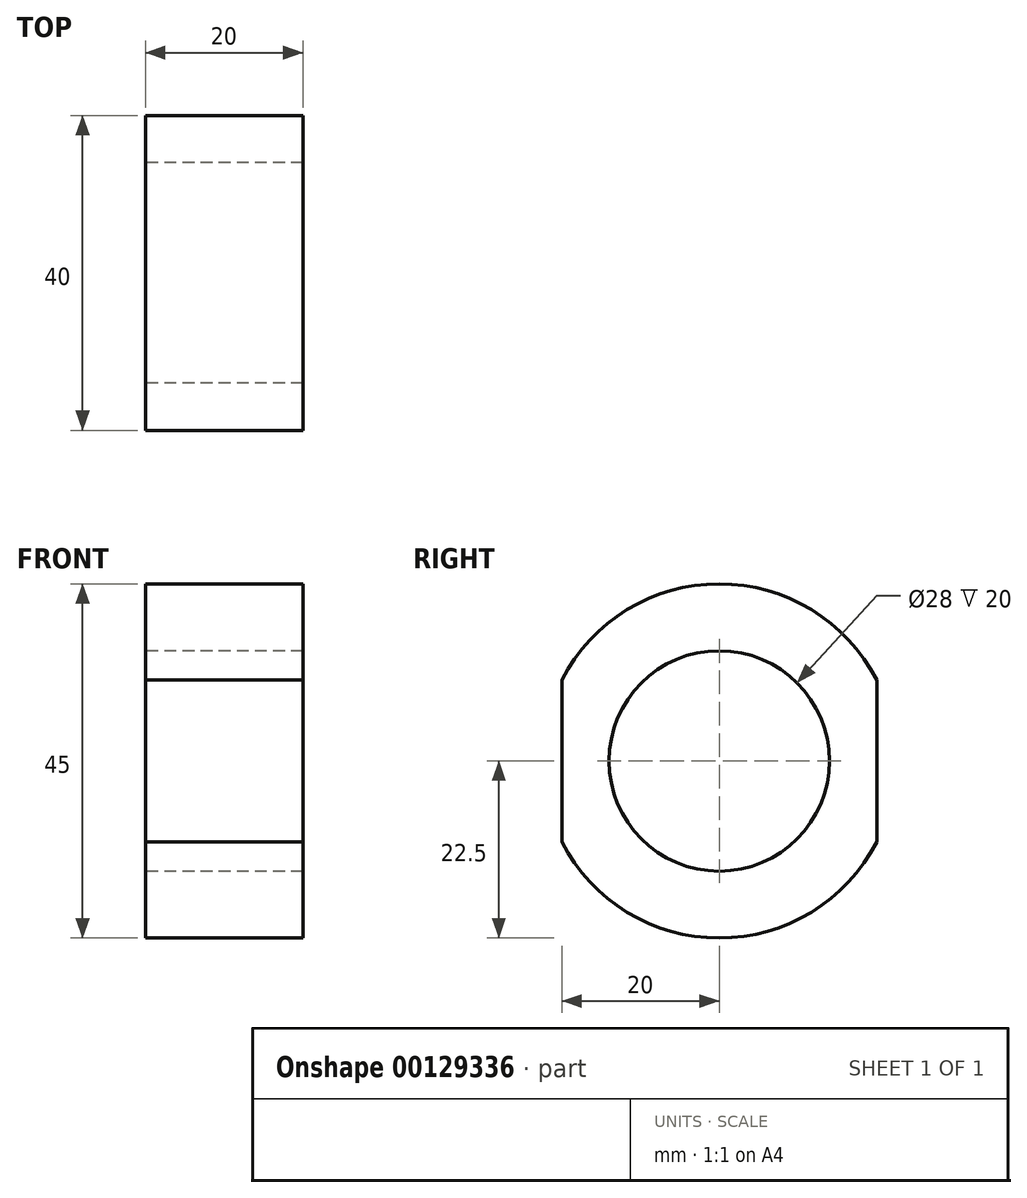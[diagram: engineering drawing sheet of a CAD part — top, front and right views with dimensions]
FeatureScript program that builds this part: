
annotation { "Feature Type Name" : "Feature", "Feature Type Description" : "" }
export const myFeature = defineFeature(function(context is Context, id is Id, definition is map)
    precondition{}
    {
        {
            var Q0;
            Q0=qCreatedBy(makeId("Right.planeOp"),FACE);
            var sketch = newSketch(context, id + "F0", { "sketchPlane" : qUnion([Q0])});
            skCircle(sketch, "E0", {"center": v(0, 0) * mm, "radius": 14 * mm});
            skArc(sketch, "E1", {"start": v(-20, -10.3) * mm, "mid": v(0, -22.5) * mm, "end": v(20, -10.3) * mm});
            skLineSegment(sketch, "E2", {"start": v(-20, 10.3) * mm, "end": v(-20, -10.3) * mm});
            skPoint(sketch, "E3.orphan", {"position": v(-20, 30.88) * mm});
            skLineSegment(sketch, "E4.MirrorCS", {"start": v(20, 10.3) * mm, "end": v(20, -10.3) * mm});
            skArc(sketch, "E5.trimOffspring", {"start": v(20, 10.3) * mm, "mid": v(0, 22.5) * mm, "end": v(-20, 10.3) * mm});
            skSolve(sketch);
        }
        {
            var Q0;
            Q0=makeQuery(id+"F0.imprint","IMPRINT",FACE,{"disambiguationData":[TD([[makeQuery(id+"F0.imprint","IMPRINT",EDGE,{"derivedFrom":sQuery(id+"F0.wireOp",EDGE,"E0")}),-1.0]])]});
            extrude(context, id + "F1", {"entities" : qUnion([Q0]), "depth" : 20 * mm});
        }
    });
